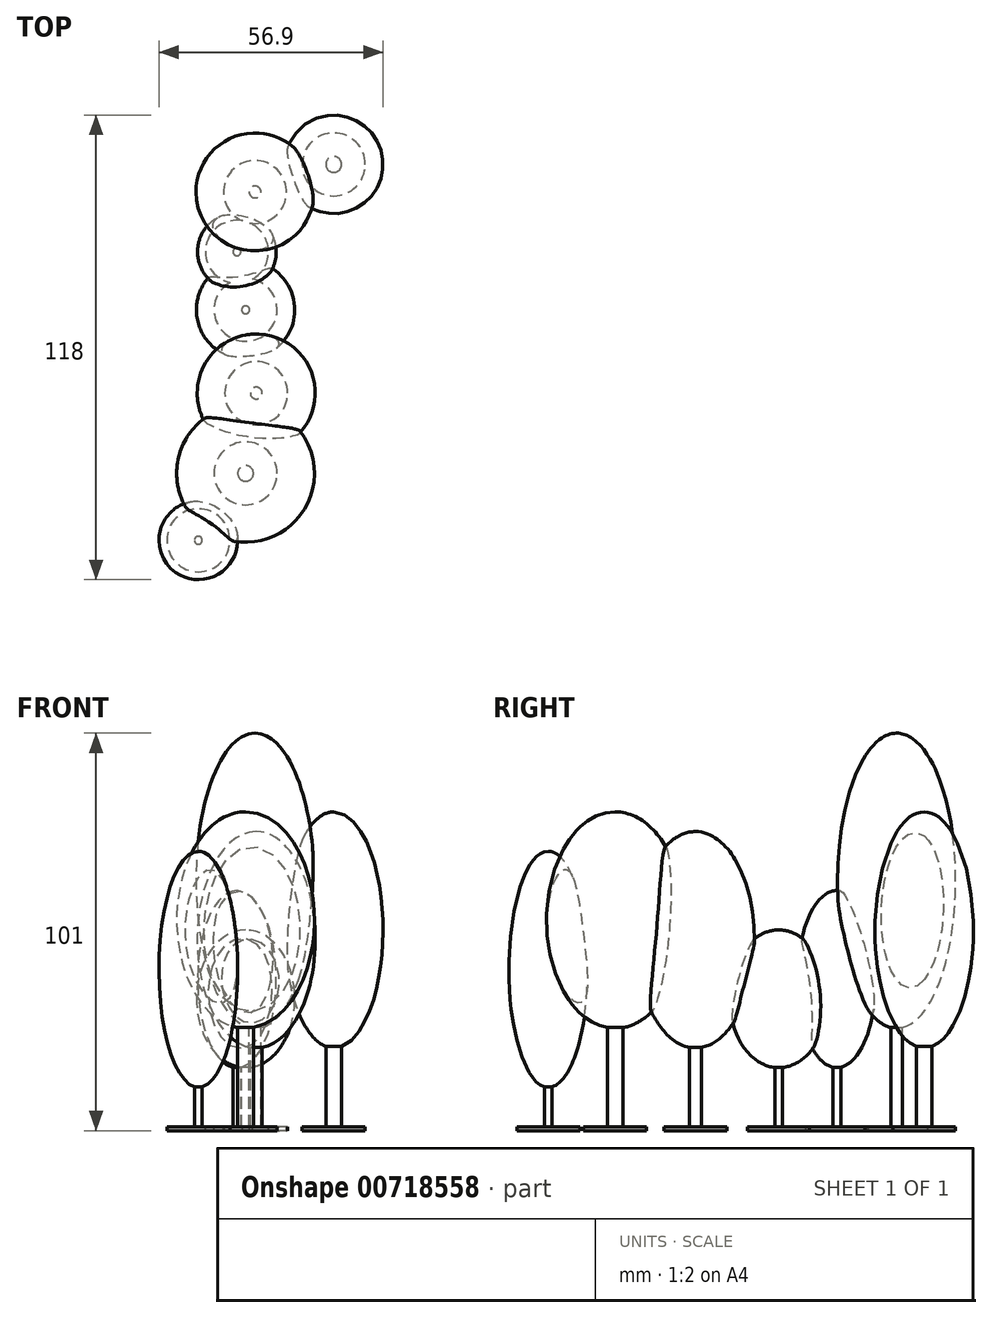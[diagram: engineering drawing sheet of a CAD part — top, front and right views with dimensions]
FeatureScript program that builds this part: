
annotation { "Feature Type Name" : "Feature", "Feature Type Description" : "" }
export const myFeature = defineFeature(function(context is Context, id is Id, definition is map)
    precondition{}
    {
        {
            var Q0;
            Q0=qCreatedBy(makeId("Top.planeOp"),FACE);
            var sketch = newSketch(context, id + "F0", { "sketchPlane" : qUnion([Q0])});
            skPoint(sketch, "E0", {"position": v(-20, -7) * mm});
            skPoint(sketch, "E1", {"position": v(-24.6, -22.2) * mm});
            skPoint(sketch, "E2", {"position": v(-19.7, -58.1) * mm});
            skPoint(sketch, "E3", {"position": v(-22.4, -36.95) * mm});
            skPoint(sketch, "E4", {"position": v(-34.4, -95.5) * mm});
            skPoint(sketch, "E5", {"position": v(-22.4, -78.5) * mm});
            skSolve(sketch);
        }
        {
            var Q0;
            Q0=sQuery(id+"F0.wireOp",VERTEX,"E0");
            var Q1;
            Q1=qCreatedBy(makeId("Front.planeOp"),FACE);
            cPlane(context, id + "F1", {"entities" : qUnion([Q0, Q1]), "cplaneType" : CPlaneType.PLANE_POINT, "offset" : 25 * mm, "width" : 150 * mm, "height" : 150 * mm});
        }
        {
            var Q0;
            Q0=sQuery(id+"F0.wireOp",VERTEX,"E1");
            var Q1;
            Q1=qCreatedBy(makeId("Front.planeOp"),FACE);
            cPlane(context, id + "F2", {"entities" : qUnion([Q0, Q1]), "cplaneType" : CPlaneType.PLANE_POINT, "offset" : 25 * mm, "width" : 150 * mm, "height" : 150 * mm});
        }
        {
            var Q0;
            Q0=sQuery(id+"F0.wireOp",VERTEX,"E3");
            var Q1;
            Q1=qCreatedBy(makeId("Front.planeOp"),FACE);
            cPlane(context, id + "F3", {"entities" : qUnion([Q0, Q1]), "cplaneType" : CPlaneType.PLANE_POINT, "offset" : 25 * mm, "width" : 150 * mm, "height" : 150 * mm});
        }
        {
            var Q0;
            Q0=sQuery(id+"F0.wireOp",VERTEX,"E2");
            var Q1;
            Q1=qCreatedBy(makeId("Front.planeOp"),FACE);
            cPlane(context, id + "F4", {"entities" : qUnion([Q0, Q1]), "cplaneType" : CPlaneType.PLANE_POINT, "offset" : 25 * mm, "width" : 150 * mm, "height" : 150 * mm});
        }
        {
            var Q0;
            Q0=sQuery(id+"F0.wireOp",VERTEX,"E5");
            var Q1;
            Q1=qCreatedBy(makeId("Front.planeOp"),FACE);
            cPlane(context, id + "F5", {"entities" : qUnion([Q0, Q1]), "cplaneType" : CPlaneType.PLANE_POINT, "offset" : 25 * mm, "width" : 150 * mm, "height" : 150 * mm});
        }
        {
            var Q0;
            Q0=sQuery(id+"F0.wireOp",VERTEX,"E4");
            var Q1;
            Q1=qCreatedBy(makeId("Front.planeOp"),FACE);
            cPlane(context, id + "F6", {"entities" : qUnion([Q0, Q1]), "cplaneType" : CPlaneType.PLANE_POINT, "offset" : 25 * mm, "width" : 150 * mm, "height" : 150 * mm});
        }
        {
            var Q0;
            Q0=qCreatedBy(makeId("Front.planeOp"),FACE);
            var sketch = newSketch(context, id + "F7", { "sketchPlane" : qUnion([Q0])});
            skEllipse(sketch, "E6", {"center": v(0, 51) * mm, "majorRadius": 30 * mm, "minorRadius": 12.5 * mm, "majorAxis": v(0, 1)});
            skLineSegment(sketch, "E7", {"start": v(0, 81) * mm, "end": v(0, 1) * mm});
            skLineSegment(sketch, "E8.top", {"start": v(-2, 1) * mm, "end": v(0, 1) * mm});
            skLineSegment(sketch, "E8.left", {"start": v(-2, 21.39) * mm, "end": v(-2, 1) * mm});
            skLineSegment(sketch, "E8.right", {"start": v(0, 21) * mm, "end": v(0, 1) * mm});
            skLineSegment(sketch, "E9.bottom", {"start": v(-8, 1) * mm, "end": v(0, 1) * mm});
            skLineSegment(sketch, "E9.top", {"start": v(-8, 0) * mm, "end": v(0, 0) * mm});
            skLineSegment(sketch, "E9.left", {"start": v(-8, 1) * mm, "end": v(-8, 0) * mm});
            skLineSegment(sketch, "E9.right", {"start": v(0, 1) * mm, "end": v(0, 0) * mm});
            skSolve(sketch);
        }
        {
            var Q0;
            Q0=qCreatedBy(id+"F1.planeOp",FACE);
            var sketch = newSketch(context, id + "F8", { "sketchPlane" : qUnion([Q0])});
            skEllipse(sketch, "E10", {"center": v(-20, 63.5) * mm, "majorRadius": 37.5 * mm, "minorRadius": 15 * mm, "majorAxis": v(0, 1)});
            skLineSegment(sketch, "E11", {"start": v(-20, 101) * mm, "end": v(-20, 1) * mm});
            skLineSegment(sketch, "E12.top", {"start": v(-21.5, 1) * mm, "end": v(-20, 1) * mm});
            skLineSegment(sketch, "E12.left", {"start": v(-21.5, 26.19) * mm, "end": v(-21.5, 1) * mm});
            skLineSegment(sketch, "E12.right", {"start": v(-20, 26) * mm, "end": v(-20, 1) * mm});
            skLineSegment(sketch, "E13.bottom", {"start": v(-28, 1) * mm, "end": v(-20, 1) * mm});
            skLineSegment(sketch, "E13.top", {"start": v(-28, 0) * mm, "end": v(-20, 0) * mm});
            skLineSegment(sketch, "E13.left", {"start": v(-28, 1) * mm, "end": v(-28, 0) * mm});
            skLineSegment(sketch, "E13.right", {"start": v(-20, 1) * mm, "end": v(-20, 0) * mm});
            skSolve(sketch);
        }
        {
            var Q0;
            Q0=qCreatedBy(id+"F2.planeOp",FACE);
            var sketch = newSketch(context, id + "F9", { "sketchPlane" : qUnion([Q0])});
            skEllipse(sketch, "E14", {"center": v(-24.6, 38.5) * mm, "majorRadius": 22.5 * mm, "minorRadius": 10 * mm, "majorAxis": v(0, 1)});
            skLineSegment(sketch, "E15", {"start": v(-24.6, 61) * mm, "end": v(-24.6, 1) * mm});
            skLineSegment(sketch, "E16.top", {"start": v(-25.6, 1) * mm, "end": v(-24.6, 1) * mm});
            skLineSegment(sketch, "E16.left", {"start": v(-25.6, 16.11) * mm, "end": v(-25.6, 1) * mm});
            skLineSegment(sketch, "E16.right", {"start": v(-24.6, 16) * mm, "end": v(-24.6, 1) * mm});
            skLineSegment(sketch, "E17.bottom", {"start": v(-32.6, 1) * mm, "end": v(-24.6, 1) * mm});
            skLineSegment(sketch, "E17.top", {"start": v(-32.6, 0) * mm, "end": v(-24.6, 0) * mm});
            skLineSegment(sketch, "E17.left", {"start": v(-32.6, 1) * mm, "end": v(-32.6, 0) * mm});
            skLineSegment(sketch, "E17.right", {"start": v(-24.6, 1) * mm, "end": v(-24.6, 0) * mm});
            skSolve(sketch);
        }
        {
            var Q0;
            Q0=qCreatedBy(id+"F3.planeOp",FACE);
            var sketch = newSketch(context, id + "F10", { "sketchPlane" : qUnion([Q0])});
            skEllipse(sketch, "E18", {"center": v(-22.4, 33.5) * mm, "majorRadius": 17.5 * mm, "minorRadius": 12.5 * mm, "majorAxis": v(0, 1)});
            skLineSegment(sketch, "E19", {"start": v(-22.4, 51) * mm, "end": v(-22.4, 1) * mm});
            skLineSegment(sketch, "E20.top", {"start": v(-23.4, 1) * mm, "end": v(-22.4, 1) * mm});
            skLineSegment(sketch, "E20.left", {"start": v(-23.4, 16.06) * mm, "end": v(-23.4, 1) * mm});
            skLineSegment(sketch, "E20.right", {"start": v(-22.4, 16) * mm, "end": v(-22.4, 1) * mm});
            skLineSegment(sketch, "E21.bottom", {"start": v(-30.4, 1) * mm, "end": v(-22.4, 1) * mm});
            skLineSegment(sketch, "E21.top", {"start": v(-30.4, 0) * mm, "end": v(-22.4, 0) * mm});
            skLineSegment(sketch, "E21.left", {"start": v(-30.4, 1) * mm, "end": v(-30.4, 0) * mm});
            skLineSegment(sketch, "E21.right", {"start": v(-22.4, 1) * mm, "end": v(-22.4, 0) * mm});
            skSolve(sketch);
        }
        {
            var Q0;
            Q0=qCreatedBy(id+"F4.planeOp",FACE);
            var sketch = newSketch(context, id + "F11", { "sketchPlane" : qUnion([Q0])});
            skEllipse(sketch, "E22", {"center": v(-19.7, 48.5) * mm, "majorRadius": 27.5 * mm, "minorRadius": 15 * mm, "majorAxis": v(0, 1)});
            skLineSegment(sketch, "E23", {"start": v(-19.7, 76) * mm, "end": v(-19.7, 1) * mm});
            skLineSegment(sketch, "E24.top", {"start": v(-21.2, 1) * mm, "end": v(-19.7, 1) * mm});
            skLineSegment(sketch, "E24.left", {"start": v(-21.2, 21.14) * mm, "end": v(-21.2, 1) * mm});
            skLineSegment(sketch, "E24.right", {"start": v(-19.7, 21) * mm, "end": v(-19.7, 1) * mm});
            skLineSegment(sketch, "E25.bottom", {"start": v(-27.7, 1) * mm, "end": v(-19.7, 1) * mm});
            skLineSegment(sketch, "E25.top", {"start": v(-27.7, 0) * mm, "end": v(-19.7, 0) * mm});
            skLineSegment(sketch, "E25.left", {"start": v(-27.7, 1) * mm, "end": v(-27.7, 0) * mm});
            skLineSegment(sketch, "E25.right", {"start": v(-19.7, 1) * mm, "end": v(-19.7, 0) * mm});
            skSolve(sketch);
        }
        {
            var Q0;
            Q0=qCreatedBy(id+"F5.planeOp",FACE);
            var sketch = newSketch(context, id + "F12", { "sketchPlane" : qUnion([Q0])});
            skEllipse(sketch, "E26", {"center": v(-22.4, 53.5) * mm, "majorRadius": 27.5 * mm, "minorRadius": 17.5 * mm, "majorAxis": v(0, 1)});
            skLineSegment(sketch, "E27", {"start": v(-22.4, 81) * mm, "end": v(-22.4, 1) * mm});
            skLineSegment(sketch, "E28.top", {"start": v(-24.4, 1) * mm, "end": v(-22.4, 1) * mm});
            skLineSegment(sketch, "E28.left", {"start": v(-24.4, 26.18) * mm, "end": v(-24.4, 1) * mm});
            skLineSegment(sketch, "E28.right", {"start": v(-22.4, 26) * mm, "end": v(-22.4, 1) * mm});
            skLineSegment(sketch, "E29.bottom", {"start": v(-30.4, 1) * mm, "end": v(-22.4, 1) * mm});
            skLineSegment(sketch, "E29.top", {"start": v(-30.4, 0) * mm, "end": v(-22.4, 0) * mm});
            skLineSegment(sketch, "E29.left", {"start": v(-30.4, 1) * mm, "end": v(-30.4, 0) * mm});
            skLineSegment(sketch, "E29.right", {"start": v(-22.4, 1) * mm, "end": v(-22.4, 0) * mm});
            skSolve(sketch);
        }
        {
            var Q0;
            Q0=qCreatedBy(id+"F6.planeOp",FACE);
            var sketch = newSketch(context, id + "F13", { "sketchPlane" : qUnion([Q0])});
            skEllipse(sketch, "E30", {"center": v(-34.4, 41) * mm, "majorRadius": 30 * mm, "minorRadius": 10 * mm, "majorAxis": v(0, 1)});
            skLineSegment(sketch, "E31", {"start": v(-34.4, 71) * mm, "end": v(-34.4, 1) * mm});
            skLineSegment(sketch, "E32.top", {"start": v(-35.4, 1) * mm, "end": v(-34.4, 1) * mm});
            skLineSegment(sketch, "E32.left", {"start": v(-35.4, 11.15) * mm, "end": v(-35.4, 1) * mm});
            skLineSegment(sketch, "E32.right", {"start": v(-34.4, 11) * mm, "end": v(-34.4, 1) * mm});
            skLineSegment(sketch, "E33.bottom", {"start": v(-42.4, 1) * mm, "end": v(-34.4, 1) * mm});
            skLineSegment(sketch, "E33.top", {"start": v(-42.4, 0) * mm, "end": v(-34.4, 0) * mm});
            skLineSegment(sketch, "E33.left", {"start": v(-42.4, 1) * mm, "end": v(-42.4, 0) * mm});
            skLineSegment(sketch, "E33.right", {"start": v(-34.4, 1) * mm, "end": v(-34.4, 0) * mm});
            skSolve(sketch);
        }
        {
            var Q0;
            {var subQ0=sQuery(id+"F7.wireOp",EDGE,"E7");Q0=makeQuery(id+"F7.imprint","IMPRINT",FACE,{"disambiguationData":[TD([[makeQuery(id+"F7.imprint","IMPRINT",EDGE,{"derivedFrom":subQ0}),-1.0]])]});}
            var Q1;
            {var subQ2=sQuery(id+"F7.wireOp",EDGE,"E8.left");Q1=makeQuery(id+"F7.imprint","IMPRINT",FACE,{"disambiguationData":[TD([[makeQuery(id+"F7.imprint","IMPRINT",EDGE,{"derivedFrom":subQ2}),1.0]])]});}
            var Q2;
            Q2=makeQuery(id+"F7.imprint","IMPRINT",FACE,{"disambiguationData":[TD([[makeQuery(id+"F7.imprint","IMPRINT",EDGE,{"derivedFrom":sQuery(id+"F7.wireOp",EDGE,"E9.top")}),1.0]])]});
            var Q3;
            Q3=sQuery(id+"F7.wireOp",EDGE,"E7");
            revolve(context, id + "F14", {"surfaceOperationType" : NewSurfaceOperationType.NEW, "entities" : qUnion([Q0, Q1, Q2]), "axis" : qUnion([Q3]), "revolveType" : RevolveType.FULL});
        }
        {
            var Q0;
            {var subQ0=sQuery(id+"F8.wireOp",EDGE,"E11");Q0=makeQuery(id+"F8.imprint","IMPRINT",FACE,{"disambiguationData":[TD([[makeQuery(id+"F8.imprint","IMPRINT",EDGE,{"derivedFrom":subQ0}),-1.0]])]});}
            var Q1;
            {var subQ2=sQuery(id+"F8.wireOp",EDGE,"E12.left");Q1=makeQuery(id+"F8.imprint","IMPRINT",FACE,{"disambiguationData":[TD([[makeQuery(id+"F8.imprint","IMPRINT",EDGE,{"derivedFrom":subQ2}),1.0]])]});}
            var Q2;
            Q2=makeQuery(id+"F8.imprint","IMPRINT",FACE,{"disambiguationData":[TD([[makeQuery(id+"F8.imprint","IMPRINT",EDGE,{"derivedFrom":sQuery(id+"F8.wireOp",EDGE,"E13.top")}),1.0]])]});
            var Q3;
            Q3=sQuery(id+"F8.wireOp",EDGE,"E11");
            revolve(context, id + "F15", {"operationType" : NewBodyOperationType.ADD, "surfaceOperationType" : NewSurfaceOperationType.NEW, "entities" : qUnion([Q0, Q1, Q2]), "axis" : qUnion([Q3]), "revolveType" : RevolveType.FULL});
        }
        {
            var Q0;
            {var subQ0=sQuery(id+"F9.wireOp",EDGE,"E15");Q0=makeQuery(id+"F9.imprint","IMPRINT",FACE,{"disambiguationData":[TD([[makeQuery(id+"F9.imprint","IMPRINT",EDGE,{"derivedFrom":subQ0}),-1.0]])]});}
            var Q1;
            {var subQ2=sQuery(id+"F9.wireOp",EDGE,"E16.left");Q1=makeQuery(id+"F9.imprint","IMPRINT",FACE,{"disambiguationData":[TD([[makeQuery(id+"F9.imprint","IMPRINT",EDGE,{"derivedFrom":subQ2}),1.0]])]});}
            var Q2;
            Q2=makeQuery(id+"F9.imprint","IMPRINT",FACE,{"disambiguationData":[TD([[makeQuery(id+"F9.imprint","IMPRINT",EDGE,{"derivedFrom":sQuery(id+"F9.wireOp",EDGE,"E17.top")}),1.0]])]});
            var Q3;
            Q3=sQuery(id+"F9.wireOp",EDGE,"E15");
            revolve(context, id + "F16", {"operationType" : NewBodyOperationType.ADD, "surfaceOperationType" : NewSurfaceOperationType.NEW, "entities" : qUnion([Q0, Q1, Q2]), "axis" : qUnion([Q3]), "revolveType" : RevolveType.FULL});
        }
        {
            var Q0;
            {var subQ0=sQuery(id+"F10.wireOp",EDGE,"E19");Q0=makeQuery(id+"F10.imprint","IMPRINT",FACE,{"disambiguationData":[TD([[makeQuery(id+"F10.imprint","IMPRINT",EDGE,{"derivedFrom":subQ0}),-1.0]])]});}
            var Q1;
            {var subQ2=sQuery(id+"F10.wireOp",EDGE,"E20.left");Q1=makeQuery(id+"F10.imprint","IMPRINT",FACE,{"disambiguationData":[TD([[makeQuery(id+"F10.imprint","IMPRINT",EDGE,{"derivedFrom":subQ2}),1.0]])]});}
            var Q2;
            Q2=makeQuery(id+"F10.imprint","IMPRINT",FACE,{"disambiguationData":[TD([[makeQuery(id+"F10.imprint","IMPRINT",EDGE,{"derivedFrom":sQuery(id+"F10.wireOp",EDGE,"E21.top")}),1.0]])]});
            var Q3;
            Q3=sQuery(id+"F10.wireOp",EDGE,"E19");
            revolve(context, id + "F17", {"operationType" : NewBodyOperationType.ADD, "surfaceOperationType" : NewSurfaceOperationType.NEW, "entities" : qUnion([Q0, Q1, Q2]), "axis" : qUnion([Q3]), "revolveType" : RevolveType.FULL});
        }
        {
            var Q0;
            {var subQ0=sQuery(id+"F11.wireOp",EDGE,"E23");Q0=makeQuery(id+"F11.imprint","IMPRINT",FACE,{"disambiguationData":[TD([[makeQuery(id+"F11.imprint","IMPRINT",EDGE,{"derivedFrom":subQ0}),-1.0]])]});}
            var Q1;
            {var subQ2=sQuery(id+"F11.wireOp",EDGE,"E24.left");Q1=makeQuery(id+"F11.imprint","IMPRINT",FACE,{"disambiguationData":[TD([[makeQuery(id+"F11.imprint","IMPRINT",EDGE,{"derivedFrom":subQ2}),1.0]])]});}
            var Q2;
            Q2=makeQuery(id+"F11.imprint","IMPRINT",FACE,{"disambiguationData":[TD([[makeQuery(id+"F11.imprint","IMPRINT",EDGE,{"derivedFrom":sQuery(id+"F11.wireOp",EDGE,"E25.top")}),1.0]])]});
            var Q3;
            Q3=sQuery(id+"F11.wireOp",EDGE,"E23");
            revolve(context, id + "F18", {"operationType" : NewBodyOperationType.ADD, "surfaceOperationType" : NewSurfaceOperationType.NEW, "entities" : qUnion([Q0, Q1, Q2]), "axis" : qUnion([Q3]), "revolveType" : RevolveType.FULL});
        }
        {
            var Q0;
            {var subQ0=sQuery(id+"F12.wireOp",EDGE,"E27");Q0=makeQuery(id+"F12.imprint","IMPRINT",FACE,{"disambiguationData":[TD([[makeQuery(id+"F12.imprint","IMPRINT",EDGE,{"derivedFrom":subQ0}),-1.0]])]});}
            var Q1;
            {var subQ2=sQuery(id+"F12.wireOp",EDGE,"E28.left");Q1=makeQuery(id+"F12.imprint","IMPRINT",FACE,{"disambiguationData":[TD([[makeQuery(id+"F12.imprint","IMPRINT",EDGE,{"derivedFrom":subQ2}),1.0]])]});}
            var Q2;
            Q2=makeQuery(id+"F12.imprint","IMPRINT",FACE,{"disambiguationData":[TD([[makeQuery(id+"F12.imprint","IMPRINT",EDGE,{"derivedFrom":sQuery(id+"F12.wireOp",EDGE,"E29.top")}),1.0]])]});
            var Q3;
            Q3=sQuery(id+"F12.wireOp",EDGE,"E27");
            revolve(context, id + "F19", {"operationType" : NewBodyOperationType.ADD, "surfaceOperationType" : NewSurfaceOperationType.NEW, "entities" : qUnion([Q0, Q1, Q2]), "axis" : qUnion([Q3]), "revolveType" : RevolveType.FULL});
        }
        {
            var Q0;
            {var subQ0=sQuery(id+"F13.wireOp",EDGE,"E31");Q0=makeQuery(id+"F13.imprint","IMPRINT",FACE,{"disambiguationData":[TD([[makeQuery(id+"F13.imprint","IMPRINT",EDGE,{"derivedFrom":subQ0}),-1.0]])]});}
            var Q1;
            {var subQ2=sQuery(id+"F13.wireOp",EDGE,"E32.left");Q1=makeQuery(id+"F13.imprint","IMPRINT",FACE,{"disambiguationData":[TD([[makeQuery(id+"F13.imprint","IMPRINT",EDGE,{"derivedFrom":subQ2}),1.0]])]});}
            var Q2;
            Q2=makeQuery(id+"F13.imprint","IMPRINT",FACE,{"disambiguationData":[TD([[makeQuery(id+"F13.imprint","IMPRINT",EDGE,{"derivedFrom":sQuery(id+"F13.wireOp",EDGE,"E33.top")}),1.0]])]});
            var Q3;
            Q3=sQuery(id+"F13.wireOp",EDGE,"E31");
            revolve(context, id + "F20", {"operationType" : NewBodyOperationType.ADD, "surfaceOperationType" : NewSurfaceOperationType.NEW, "entities" : qUnion([Q0, Q1, Q2]), "axis" : qUnion([Q3]), "revolveType" : RevolveType.FULL});
        }
    });
